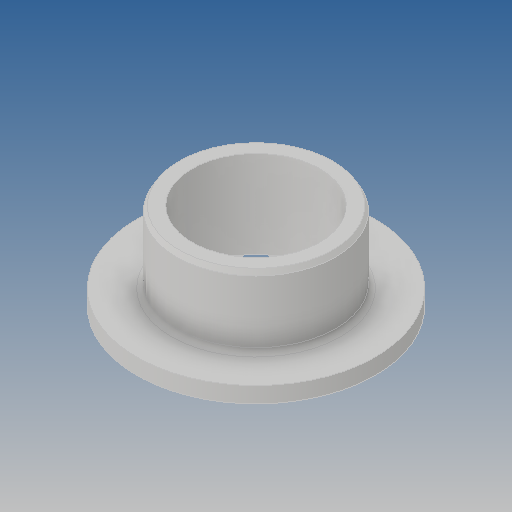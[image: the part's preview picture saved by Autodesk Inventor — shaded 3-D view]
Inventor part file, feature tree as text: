
AUTODESK INVENTOR PART (.ipt)
format: ipt  version: 2018 (Build 220112000, 112)  size: 129,024 bytes
history: native  units: mm
features: fillet x1
ambient origin geometry x8: Origin, YZ Plane, XZ Plane, XY Plane, X Axis, Y Axis, Z Axis, Center Point
bodies: Solid1 (feature_tree)
feature tree (1):
  fillet  "Fillet1"  [1 undecoded]
note: 1 required parameter value undecoded (feature->parameter linkage not recoverable at this tier; creation-order binding heuristic only, values carry confidence <= 0.55)
